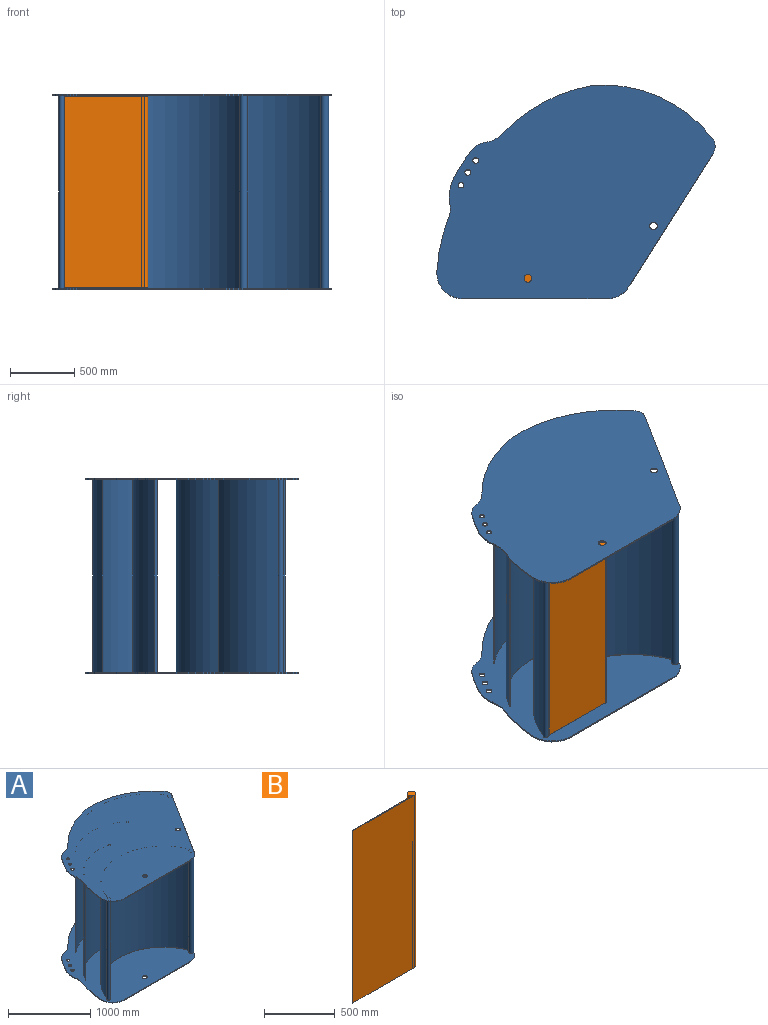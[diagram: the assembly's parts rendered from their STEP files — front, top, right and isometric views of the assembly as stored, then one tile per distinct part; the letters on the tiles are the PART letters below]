
ASSEMBLY  parts=2 mates=2
PART A: 61 faces, bbox 2164.2x1661x1520 mm
  f0: cylinder r=30.5mm len=61mm, axis (0,0,-1), area 1916.4mm2, adj f48,f49
  f1: cylinder r=29.5mm len=59mm, axis (0,0,-1), area 1853.5mm2, adj f48,f49
  f2: cylinder r=22mm len=44mm, axis (0,0,-1), area 1382.3mm2, adj f48,f49
  f3: cylinder r=22mm len=44mm, axis (0,0,-1), area 1382.3mm2, adj f48,f49
  f4: cylinder r=22mm len=44mm, axis (0,0,-1), area 1382.3mm2, adj f48,f49
  f5: cylinder r=326.18mm len=176.61mm, axis (0,0,-1), area 1797.7mm2, adj f48,f49,f50,f60
  f6: cylinder r=200mm len=212.82mm, axis (0,0,-1), area 3269.9mm2, adj f48,f49,f51,f52
  f7: cylinder r=20.5mm len=1500mm, axis (0,0,-1), area 183146.8mm2, adj f30,f44,f45,f49
  f8: cylinder r=30.5mm len=1500mm, axis (0,0,-1), area 272705.4mm2, adj f30,f44,f45,f46,f47,f49
  f9: cylinder r=15.5mm len=1500mm, axis (0,0,-1), area 135747.8mm2, adj f30,f41,f43,f49
  f10: cylinder r=15.5mm len=1500mm, axis (0,0,-1), area 136340.4mm2, adj f30,f37,f40,f49
  f11: cylinder r=30.5mm len=1500mm, axis (0,0,-1), area 274743.1mm2, adj f30,f32,f34,f35,f36,f49
  f12: cylinder r=30.5mm len=61mm, axis (0,0,-1), area 1916.4mm2, adj f30,f31
  f13: cylinder r=22mm len=44mm, axis (0,0,-1), area 1382.3mm2, adj f30,f31
  f14: cylinder r=22mm len=44mm, axis (0,0,-1), area 1382.3mm2, adj f30,f31
  f15: cylinder r=22mm len=44mm, axis (0,0,-1), area 1382.3mm2, adj f30,f31
  f16: cylinder r=29.5mm len=59mm, axis (0,0,-1), area 1853.5mm2, adj f30,f31
  f17: cylinder r=326.18mm len=176.61mm, axis (0,0,-1), area 1797.7mm2, adj f28,f29,f30,f31
  f18: cylinder r=200mm len=212.82mm, axis (0,0,-1), area 3269.9mm2, adj f19,f20,f30,f31
  f19: cylinder r=1403.06mm len=415.74mm, axis (0,0,-1), area 4273.2mm2, adj f18,f29,f30,f31
  f20: plane 1123.76x10mm, normal (0,-1,0), area 11237.6mm2, adj f18,f21,f30,f31
  f21: cylinder r=200mm len=169mm, axis (0,0,-1), area 2013.2mm2, adj f20,f22,f30,f31
  f22: plane 1036.5x655.9mm, normal (0.85,-0.53,0), area 12265.9mm2, adj f21,f23,f30,f31,f36,f47
  f23: cylinder r=100mm len=114.68mm, axis (0,0,-1), area 1222.9mm2, adj f22,f24,f30,f31
  f24: cylinder r=1074.34mm len=926.41mm, axis (0,0,-1), area 10568mm2, adj f23,f25,f30,f31
  f25: cylinder r=1282.61mm len=713.26mm, axis (0,0,-1), area 8227.7mm2, adj f24,f26,f30,f31
  f26: cylinder r=200mm len=117.51mm, axis (0,0,-1), area 1346.6mm2, adj f25,f27,f30,f31
  f27: cylinder r=186.95mm len=116.81mm, axis (0,0,-1), area 1363.1mm2, adj f26,f28,f30,f31
  f28: cylinder r=1324.47mm len=239.75mm, axis (0,0,-1), area 2828.3mm2, adj f17,f27,f30,f31
  f29: cylinder r=200mm len=107.43mm, axis (0,0,-1), area 1093.1mm2, adj f17,f19,f30,f31
  f30: plane 2164.16x1660.98mm, normal (0,0,1), area 2565292.9mm2, adj f7,f8,f9,f10,f11,f12,f13,f14
  f31: plane 2164.16x1660.98mm, normal (0,0,-1), area 2603609.2mm2, adj f12,f13,f14,f15,f16,f17,f18,f19
  f32: cylinder r=883.17mm len=1500mm, axis (0,0,-1), area 1936048.7mm2, adj f11,f30,f33,f49
  f33: plane 1500x5.5mm, normal (-0.92,-0.4,0), area 9000mm2, adj f30,f32,f34,f49
  f34: cylinder r=877.17mm len=1500mm, axis (0,0,-1), area 1914005.6mm2, adj f11,f30,f33,f49
  f35: plane 9.3x5.88mm, normal (0,0,1), area 3.7mm2, adj f11,f54
  f36: plane 9.3x5.88mm, normal (0,0,-1), area 3.7mm2, adj f11,f22
  f37: cylinder r=685.89mm len=1500mm, axis (0,0,-1), area 1444091.5mm2, adj f10,f30,f38,f49
  f38: plane 1500x4.62mm, normal (-0.77,-0.64,0), area 9000mm2, adj f30,f37,f39,f49
  f39: plane 1500x0.08mm, normal (0.65,-0.76,0), area 152.6mm2, adj f30,f38,f40,f49
  f40: cylinder r=679.89mm len=1500mm, axis (0,0,-1), area 1427930.9mm2, adj f10,f30,f39,f49
  f41: cylinder r=640.37mm len=1500mm, axis (0,0,-1), area 1242581.2mm2, adj f9,f30,f42,f49
  f42: plane 1500x5.24mm, normal (-0.49,-0.87,0), area 9000mm2, adj f30,f41,f43,f49
  f43: cylinder r=634.37mm len=1500mm, axis (0,0,-1), area 1226053.6mm2, adj f9,f30,f42,f49
  f44: cylinder r=755.25mm len=1500mm, axis (0,0,-1), area 2799788.5mm2, adj f7,f8,f30,f49
  f45: cylinder r=761.25mm len=1500mm, axis (0,0,-1), area 2838096.4mm2, adj f7,f8,f30,f49
  f46: plane 9.3x5.88mm, normal (0,0,1), area 3.7mm2, adj f8,f54
  f47: plane 9.3x5.88mm, normal (0,0,-1), area 3.7mm2, adj f8,f22
  f48: plane 2164.16x1660.98mm, normal (0,0,1), area 2603609.2mm2, adj f0,f1,f2,f3,f4,f5,f6,f50
  f49: plane 2164.16x1660.98mm, normal (0,0,-1), area 2565292.9mm2, adj f0,f1,f2,f3,f4,f5,f6,f7
  f50: cylinder r=200mm len=107.43mm, axis (0,0,-1), area 1093.1mm2, adj f5,f48,f49,f51
  f51: cylinder r=1403.06mm len=415.74mm, axis (0,0,-1), area 4273.2mm2, adj f6,f48,f49,f50
  f52: plane 1123.76x10mm, normal (0,-1,0), area 11237.6mm2, adj f6,f48,f49,f53
  f53: cylinder r=200mm len=169mm, axis (0,0,-1), area 2013.2mm2, adj f48,f49,f52,f54
  f54: plane 1036.5x655.9mm, normal (0.85,-0.53,0), area 12265.9mm2, adj f35,f46,f48,f49,f53,f55
  f55: cylinder r=100mm len=114.68mm, axis (0,0,-1), area 1222.9mm2, adj f48,f49,f54,f56
  f56: cylinder r=1074.34mm len=926.41mm, axis (0,0,-1), area 10568mm2, adj f48,f49,f55,f57
  f57: cylinder r=1282.61mm len=713.26mm, axis (0,0,-1), area 8227.7mm2, adj f48,f49,f56,f58
  f58: cylinder r=200mm len=117.51mm, axis (0,0,-1), area 1346.6mm2, adj f48,f49,f57,f59
  f59: cylinder r=186.95mm len=116.81mm, axis (0,0,-1), area 1363.1mm2, adj f48,f49,f58,f60
  f60: cylinder r=1324.47mm len=239.75mm, axis (0,0,-1), area 2828.3mm2, adj f5,f48,f49,f59
PART B: 6 faces, bbox 646.3x61x1490 mm
  f0: cylinder r=30.5mm len=1490mm, axis (0,0,-1), area 256544.7mm2, adj f1,f2,f4,f5
  f1: plane 1490x615.77mm, normal (0,-1,0), area 917501.9mm2, adj f0,f3,f4,f5
  f2: plane 1490x597.61mm, normal (0,1,0), area 890434.7mm2, adj f0,f3,f4,f5
  f3: plane 1490x6mm, normal (-1,0,0), area 8940mm2, adj f1,f2,f4,f5
  f4: plane 646.27x61mm, normal (0,0,1), area 6542.9mm2, adj f0,f1,f2,f3
  f5: plane 646.27x61mm, normal (0,0,-1), area 6542.9mm2, adj f0,f1,f2,f3
PLACE A t=(0,0,-10)mm
PLACE B rot(axis=(0,0,-1),0deg) t=(0,0,-10)mm
MATE planar A.f0 <-> B.f0  axis (0,0,-1) through (-975.48,-407.66,750)mm
MATE revolute A.f0 <-> B.f0  axis (0,0,-1) through (-975.48,-407.66,750)mm
